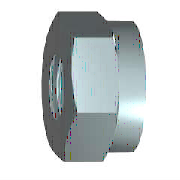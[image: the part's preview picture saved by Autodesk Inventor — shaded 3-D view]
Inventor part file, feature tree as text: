
AUTODESK INVENTOR PART (.ipt)
format: ipt  version: 2018 (Build 220112000, 112)  size: 176,640 bytes
history: native  units: mm (DEFAULTED — no unit token found)
features: sketch x4, extrude x1, chamfer x1, hole x1, other x1, plane x1
ambient origin geometry x7: Origin, YZ Plane, XZ Plane, X Axis, Y Axis, Z Axis, Center Point
bodies: Solid1 (feature_tree), Body (feature_tree)
feature tree (9):
  extrude  "Ring"  Depth=2.4mm
  chamfer  "Chamfer1"  Distance=4.6mm
  hole  "Thread"  [1 undecoded]
  other  "Work Axis1"
  plane  "Work Plane1"
  sketch  "Sketch1"  dims[d0=6.350853mm d1=2.4mm]
  sketch  "Sketch3"  dims[d3=30.0deg]
  sketch  "Sketch2"  dims[d2=0.0mm]
  sketch  "Sketch4"  dims[d4=30.0deg d5=4.6mm d6=4.6mm d26=90.0deg d7=4.6mm d8=1.6mm d9=0.0mm d30=2.459mm d31=6.0mm d32=4.0mm d33=2.0mm d34=14.3117mm d35=8.0mm d36=20.594885mm d10=0.270633mm d11=30.0deg d12=0.270633mm d13=30.0deg d14=0.0mm d15=0.0mm d45=0.0mm d46=0.270633mm d47=0.270633mm d48=0.0mm]
note: 1 required parameter value undecoded (feature->parameter linkage not recoverable at this tier; creation-order binding heuristic only, values carry confidence <= 0.55)
